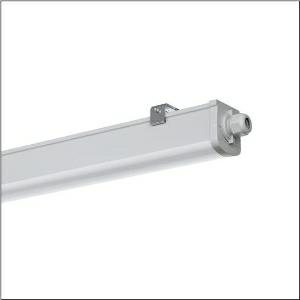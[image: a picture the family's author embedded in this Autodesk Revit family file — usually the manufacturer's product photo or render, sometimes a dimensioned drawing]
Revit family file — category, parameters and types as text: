
# Revit family: monsun_r__31_51fa207d420b_180d
name_source: partatom
category: Lighting Fixtures
units: mm (PartAtom-declared; Revit-internal decimal feet)

## family parameters
Cut with Voids When Loaded = No
Host = Face
Light Source = No
Part Type = Normal
Room Calculation Point = No
Round Connector Dimension = Use Diameter
Shared = No

## types (1)
- Monsun® 31 (1 x LED, 2300 lm, 19 W, 4000K)
    Apparent Load = 19 VA
    CIE Flux Codes = 42 72 91 92 100
    Color Rendering = 80
    Color Temperature = 4000K
    Default Elevation = 1800 mm
    Description = Monsun® 31, damp-proof luminaire, primary optical cover: diffuser, of PC, frosted, light emission: direct distribution, primary light characteristic: symmetric, installation type: surface-mounted, LED, rated luminous flux: 2.300lm, luminous efficacy: 121lm/W, light colour: 840, colour temperature: 4000K, control gear: ECG, with terminal, 3+1-pole, max. 2.5mm², through-wiring: 3x 2.5mm² + 1x 1.5mm², mains connection: 220..240V, AC, 50/60Hz, rated input power: 19W, housing, luminaire housing, of PC, light grey (RAL 7035), length: 558mm, width: 68mm, height: 76mm, protection rating (complete): IP66, insulation class (complete): insulation class II (safety insulation), certification: CE, ENEC, UKCA, protection symbol: D, impact resistance: IK08, permissible operating ambient temperature: -20..+40°C, corresponds to IFS (International Featured Standards) requirements for safety and quality in the food industry, packaging unit: 1 piece
    Height = 77 mm
    Lamp = 1 x LED
    Lamp Light Flux = 2300 lm
    Lamp Power = 19 W
    Lamp count = 1
    Length = 618 mm
    Luminous efficacy = 121 lm/W
    Manufacturer = Siteco
    ModVariant = No
    Model = 51FA207D420B
    Mounting Place = Ceiling
    Mounting Type = Surface mounted
    Number of Poles = 1
    OnlyDefault = Yes
    Power Factor = 1
    Product Name = Monsun® 31
    Product group = damp-proof luminaire | ceiling mounted
    ProductGroupID = 300
    Protection Class = Protection class II
    Protection Degree = IP 66
    RLX_Detail_Level = 1
    RlxData = <blob elided: 32553 chars, md5=7ac8e73d>
    Socket = socket
    Standby Power = 0 W
    System Light Flux = 2300 lm
    System Power = 19 W
    Type Comments = Product without accessories
    Type Image = l_1006174.jpg
    URL = http://relux.com
    VarID = ---
    Voltage = 0 V
    Weight = 0.00 kg
    Width = 69 mm

## geometry (parser evidence)
native form markers: Blend x4, Sweep x11
no freeform markers — native parametric forms only
